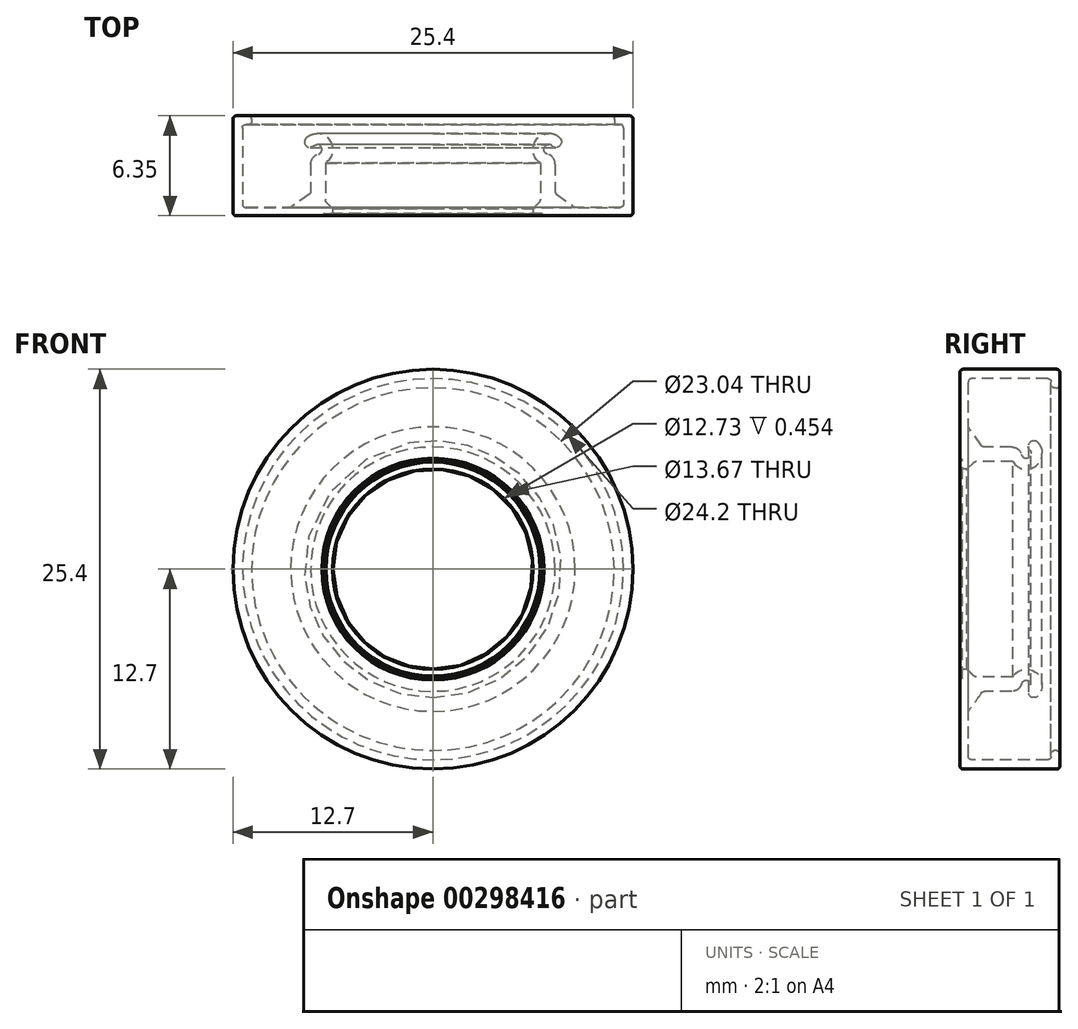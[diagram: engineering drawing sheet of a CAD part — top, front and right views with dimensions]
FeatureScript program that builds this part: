
annotation { "Feature Type Name" : "Feature", "Feature Type Description" : "" }
export const myFeature = defineFeature(function(context is Context, id is Id, definition is map)
    precondition{}
    {
        {
            var Q0;
            Q0=qCreatedBy(makeId("Top.planeOp"),FACE);
            var sketch = newSketch(context, id + "F0", { "sketchPlane" : qUnion([Q0])});
            skLineSegment(sketch, "E0", {"start": v(0, 0.46) * mm, "end": v(0, 7.99) * mm});
            skLineSegment(sketch, "E1", {"start": v(-11.52, 6.14) * mm, "end": v(-11.52, 6) * mm});
            skLineSegment(sketch, "E2", {"start": v(-11.73, 5.8) * mm, "end": v(-11.9, 5.8) * mm});
            skLineSegment(sketch, "E3", {"start": v(-12.1, 5.58) * mm, "end": v(-12.1, 0.74) * mm});
            skLineSegment(sketch, "E4", {"start": v(-11.9, 0.53) * mm, "end": v(-9.04, 0.53) * mm});
            skLineSegment(sketch, "E5", {"start": v(-9.04, 0.53) * mm, "end": v(-7.85, 1.37) * mm});
            skLineSegment(sketch, "E6", {"start": v(-7.76, 1.55) * mm, "end": v(-7.76, 3.29) * mm});
            skLineSegment(sketch, "E7", {"start": v(-11.73, 6.35) * mm, "end": v(-12.5, 6.35) * mm});
            skLineSegment(sketch, "E8", {"start": v(-12.7, 6.14) * mm, "end": v(-12.7, 0.2) * mm});
            skLineSegment(sketch, "E9", {"start": v(-12.5, 0) * mm, "end": v(-7.05, 0) * mm});
            skArc(sketch, "E10", {"start": v(-6.83, 3.35) * mm, "mid": v(-6.55, 4.82) * mm, "end": v(-8.05, 4.95) * mm});
            skArc(sketch, "E11", {"start": v(-7.28, 3.91) * mm, "mid": v(-7.09, 4.36) * mm, "end": v(-7.57, 4.44) * mm});
            skArc(sketch, "E12", {"start": v(-7.28, 3.91) * mm, "mid": v(-7.63, 3.68) * mm, "end": v(-7.76, 3.29) * mm});
            skArc(sketch, "E13", {"start": v(-8.05, 4.95) * mm, "mid": v(-8.06, 4.46) * mm, "end": v(-7.57, 4.44) * mm});
            skLineSegment(sketch, "E14", {"start": v(-6.37, 0) * mm, "end": v(-6.8, 0) * mm});
            skLineSegment(sketch, "E15", {"start": v(-6.8, 0) * mm, "end": v(-6.92, 0.15) * mm});
            skLineSegment(sketch, "E16", {"start": v(-6.92, 0.15) * mm, "end": v(-7.05, 0) * mm});
            skLineSegment(sketch, "E17", {"start": v(-6.37, 0) * mm, "end": v(-6.37, 0.45) * mm});
            skLineSegment(sketch, "E18", {"start": v(-6.37, 0.45) * mm, "end": v(-6.78, 0.88) * mm});
            skLineSegment(sketch, "E19", {"start": v(-6.83, 1.02) * mm, "end": v(-6.83, 3.35) * mm});
            skPoint(sketch, "E20.visualSharp", {"position": v(-12.1, 0.53) * mm});
            skArc(sketch, "E20.filletArc", {"start": v(-12.1, 0.74) * mm, "mid": v(-12.04, 0.59) * mm, "end": v(-11.9, 0.53) * mm});
            skPoint(sketch, "E21.visualSharp", {"position": v(-12.7, 0) * mm});
            skArc(sketch, "E21.filletArc", {"start": v(-12.7, 0.2) * mm, "mid": v(-12.64, 0.06) * mm, "end": v(-12.5, 0) * mm});
            skPoint(sketch, "E22.visualSharp", {"position": v(-12.7, 6.35) * mm});
            skArc(sketch, "E22.filletArc", {"start": v(-12.5, 6.35) * mm, "mid": v(-12.64, 6.29) * mm, "end": v(-12.7, 6.14) * mm});
            skPoint(sketch, "E23.visualSharp", {"position": v(-11.52, 6.35) * mm});
            skArc(sketch, "E23.filletArc", {"start": v(-11.52, 6.14) * mm, "mid": v(-11.58, 6.29) * mm, "end": v(-11.73, 6.35) * mm});
            skPoint(sketch, "E24.visualSharp", {"position": v(-12.1, 5.8) * mm});
            skArc(sketch, "E24.filletArc", {"start": v(-11.9, 5.8) * mm, "mid": v(-12.04, 5.73) * mm, "end": v(-12.1, 5.58) * mm});
            skPoint(sketch, "E25.visualSharp", {"position": v(-11.52, 5.8) * mm});
            skArc(sketch, "E25.filletArc", {"start": v(-11.73, 5.8) * mm, "mid": v(-11.58, 5.86) * mm, "end": v(-11.52, 6) * mm});
            skPoint(sketch, "E26.visualSharp", {"position": v(-7.76, 1.44) * mm});
            skArc(sketch, "E26.filletArc", {"start": v(-7.85, 1.37) * mm, "mid": v(-7.78, 1.45) * mm, "end": v(-7.76, 1.55) * mm});
            skPoint(sketch, "E27.visualSharp", {"position": v(-6.83, 0.94) * mm});
            skArc(sketch, "E27.filletArc", {"start": v(-6.83, 1.02) * mm, "mid": v(-6.82, 0.94) * mm, "end": v(-6.78, 0.88) * mm});
            skSolve(sketch);
        }
        {
            var Q0;
            Q0=makeQuery(id+"F0.imprint","IMPRINT",FACE,{"disambiguationData":[TD([[makeQuery(id+"F0.imprint","IMPRINT",EDGE,{"derivedFrom":sQuery(id+"F0.wireOp",EDGE,"E1")}),-1.0]])]});
            var Q1;
            Q1=sQuery(id+"F0.wireOp",EDGE,"E0");
            revolve(context, id + "F1", {"entities" : qUnion([Q0]), "axis" : qUnion([Q1]), "revolveType" : RevolveType.FULL});
        }
    });
